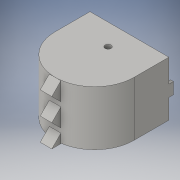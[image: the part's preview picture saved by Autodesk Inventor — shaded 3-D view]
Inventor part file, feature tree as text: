
AUTODESK INVENTOR PART (.ipt)
format: ipt  version: 2016 (Build 200138000, 138)  size: 206,336 bytes
history: native  units: in
note: dims shown in document units (in); Inventor stores cm internally (conversion verified against a paired STEP export)
features: sketch x8, extrude x7, reference x6, plane x1
ambient origin geometry x8: Origin, YZ Plane, XZ Plane, XY Plane, X Axis, Y Axis, Z Axis, Center Point
bodies: Solid1 (feature_tree)
feature tree (22):
  extrude  "Extrusion1"  Depth=1.5in TaperAngle=0.0deg
  extrude  "Extrusion2"  Depth=0.1969in TaperAngle=0.0deg
  extrude  "Extrusion3"  [1 undecoded]
  extrude  "Extrusion4"  Depth=0.3937in
  plane  "Work Plane1"
  sketch  "Sketch5"  dims[d12=1.9685in d14=0.9774in d15=0.3937in d17=1.0in d19=0.5in d20=0.0in]
  extrude  "Extrusion5"  Depth=0.5in TaperAngle=0.0deg
  extrude  "Extrusion6"  Depth=100.0in TaperAngle=0.0deg
  extrude  "Extrusion7"  [1 undecoded]
  sketch  "Sketch1"  dims[d0=0.1969in d1=1.5in d2=0.0in]
  reference  "Reference1"
  sketch  "Sketch2"  dims[d3=4.6969in d4=0.0in d5=0.1969in d6=0.0in]
  sketch  "Sketch3"  dims[d7=0.1969in d8=0.0in d9=-1.697in]
  sketch  "Sketch4"  dims[d10=0.7874in d11=0.3937in]
  reference  "Reference2"
  sketch  "Sketch6"  dims[d21=0.197in d22=0.0in d23=100.0in d24=0.0in]
  sketch  "Sketch8"
  reference  "Reference3"
  reference  "Reference4"
  reference  "Reference5"
  reference  "Reference6"
  sketch  "Sketch9"
note: 2 required parameter values undecoded (feature->parameter linkage not recoverable at this tier; creation-order binding heuristic only, values carry confidence <= 0.55)
